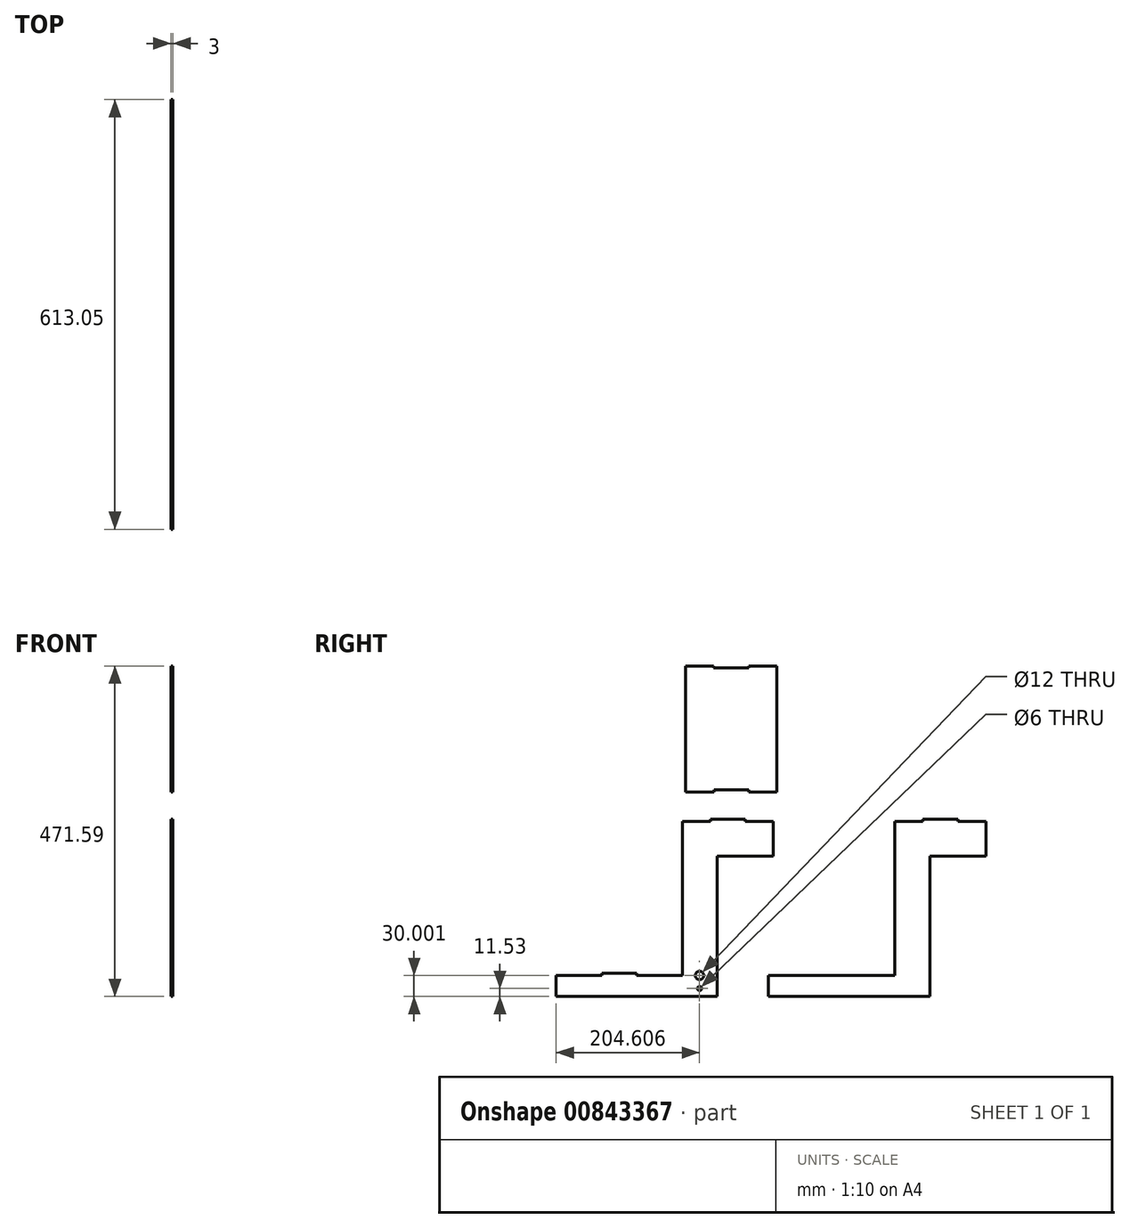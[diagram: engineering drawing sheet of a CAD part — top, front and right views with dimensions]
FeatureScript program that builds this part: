
annotation { "Feature Type Name" : "Feature", "Feature Type Description" : "" }
export const myFeature = defineFeature(function(context is Context, id is Id, definition is map)
    precondition{}
    {
        {
            var Q0;
            Q0=qCreatedBy(makeId("Right.planeOp"),FACE);
            var sketch = newSketch(context, id + "F0", { "sketchPlane" : qUnion([Q0])});
            skLineSegment(sketch, "E0", {"start": v(0, 42.16) * mm, "end": v(40, 42.16) * mm});
            skLineSegment(sketch, "E1", {"start": v(130, 42.16) * mm, "end": v(130, -7.84) * mm});
            skLineSegment(sketch, "E2", {"start": v(50, -7.84) * mm, "end": v(130, -7.84) * mm});
            skLineSegment(sketch, "E3", {"start": v(50, -7.84) * mm, "end": v(50, -207.84) * mm});
            skLineSegment(sketch, "E4", {"start": v(50, -207.84) * mm, "end": v(-180, -207.84) * mm});
            skLineSegment(sketch, "E5", {"start": v(-180, -207.84) * mm, "end": v(-180, -177.84) * mm});
            skLineSegment(sketch, "E6", {"start": v(0, -177.84) * mm, "end": v(-180, -177.84) * mm});
            skLineSegment(sketch, "E7", {"start": v(0, -177.84) * mm, "end": v(0, 42.16) * mm});
            skLineSegment(sketch, "E8", {"start": v(-298.05, 42.16) * mm, "end": v(-263.05, 42.16) * mm});
            skLineSegment(sketch, "E9", {"start": v(-173.05, 37.16) * mm, "end": v(-173.05, -2.84) * mm});
            skLineSegment(sketch, "E10", {"start": v(-248.05, -7.84) * mm, "end": v(-178.05, -7.84) * mm});
            skLineSegment(sketch, "E11", {"start": v(-253.05, -12.84) * mm, "end": v(-253.05, -207.84) * mm});
            skLineSegment(sketch, "E12", {"start": v(-253.05, -207.84) * mm, "end": v(-483.05, -207.84) * mm});
            skLineSegment(sketch, "E13", {"start": v(-483.05, -207.84) * mm, "end": v(-483.05, -177.84) * mm});
            skLineSegment(sketch, "E14", {"start": v(-303.05, -177.84) * mm, "end": v(-368.05, -177.84) * mm});
            skLineSegment(sketch, "E15", {"start": v(-303.05, -177.84) * mm, "end": v(-303.05, 37.16) * mm});
            skCircle(sketch, "E16", {"center": v(-278.44, -177.84) * mm, "radius": 6 * mm});
            skLineSegment(sketch, "E17.bottom", {"start": v(-298.36, 83.75) * mm, "end": v(-258.01, 83.75) * mm});
            skLineSegment(sketch, "E17.left", {"start": v(-298.36, 83.75) * mm, "end": v(-298.36, 263.75) * mm});
            skLineSegment(sketch, "E17.right", {"start": v(-168.36, 83.75) * mm, "end": v(-168.36, 263.75) * mm});
            skCircle(sketch, "E18", {"center": v(-278.44, -196.31) * mm, "radius": 3 * mm});
            skLineSegment(sketch, "E19", {"start": v(-263.05, 42.16) * mm, "end": v(-263.05, 45.16) * mm});
            skLineSegment(sketch, "E20", {"start": v(-263.05, 45.16) * mm, "end": v(-213.05, 45.16) * mm});
            skLineSegment(sketch, "E21", {"start": v(-213.05, 45.16) * mm, "end": v(-213.05, 42.16) * mm});
            skLineSegment(sketch, "E22.trimOffspring", {"start": v(-213.05, 42.16) * mm, "end": v(-178.05, 42.16) * mm});
            skLineSegment(sketch, "E23.top", {"start": v(-258.01, 86.75) * mm, "end": v(-208.01, 86.75) * mm});
            skLineSegment(sketch, "E23.left", {"start": v(-258.01, 83.75) * mm, "end": v(-258.01, 86.75) * mm});
            skLineSegment(sketch, "E23.right", {"start": v(-208.01, 83.75) * mm, "end": v(-208.01, 86.75) * mm});
            skLineSegment(sketch, "E24.trimOffspring", {"start": v(-208.01, 83.75) * mm, "end": v(-168.36, 83.75) * mm});
            skPoint(sketch, "E25.visualSharp", {"position": v(-303.05, 42.16) * mm});
            skPoint(sketch, "E26.visualSharp", {"position": v(-173.05, 42.16) * mm});
            skPoint(sketch, "E27.visualSharp", {"position": v(-173.05, -7.84) * mm});
            skPoint(sketch, "E28.visualSharp", {"position": v(-253.05, -7.84) * mm});
            skLineSegment(sketch, "E29", {"start": v(-483.05, -177.84) * mm, "end": v(-418.05, -177.84) * mm});
            skLineSegment(sketch, "E30", {"start": v(-418.05, -177.84) * mm, "end": v(-418.05, -174.84) * mm});
            skLineSegment(sketch, "E31", {"start": v(-418.05, -174.84) * mm, "end": v(-368.05, -174.84) * mm});
            skLineSegment(sketch, "E32", {"start": v(-368.05, -174.84) * mm, "end": v(-368.05, -177.84) * mm});
            skLineSegment(sketch, "E33.trimOffspring", {"start": v(-418.05, -177.84) * mm, "end": v(-483.05, -177.84) * mm});
            skLineSegment(sketch, "E34", {"start": v(-303.05, 37.16) * mm, "end": v(-303.05, 42.16) * mm});
            skLineSegment(sketch, "E35", {"start": v(-303.05, 42.16) * mm, "end": v(-298.05, 42.16) * mm});
            skLineSegment(sketch, "E36", {"start": v(-173.05, -2.84) * mm, "end": v(-173.05, -7.84) * mm});
            skLineSegment(sketch, "E37", {"start": v(-178.05, -7.84) * mm, "end": v(-173.05, -7.84) * mm});
            skLineSegment(sketch, "E38", {"start": v(-248.05, -7.84) * mm, "end": v(-253.05, -7.84) * mm});
            skLineSegment(sketch, "E39", {"start": v(-253.05, -12.84) * mm, "end": v(-253.05, -7.84) * mm});
            skLineSegment(sketch, "E40", {"start": v(-178.05, 42.16) * mm, "end": v(-173.05, 42.16) * mm});
            skLineSegment(sketch, "E41", {"start": v(-173.05, 42.16) * mm, "end": v(-173.05, 37.16) * mm});
            skLineSegment(sketch, "E42", {"start": v(-298.36, 263.75) * mm, "end": v(-258.36, 263.75) * mm});
            skLineSegment(sketch, "E43", {"start": v(-258.36, 263.75) * mm, "end": v(-258.36, 260.75) * mm});
            skLineSegment(sketch, "E44", {"start": v(-258.36, 260.75) * mm, "end": v(-208.36, 260.75) * mm});
            skLineSegment(sketch, "E45", {"start": v(-208.36, 260.75) * mm, "end": v(-208.36, 263.75) * mm});
            skLineSegment(sketch, "E46.trimOffspring", {"start": v(-208.36, 263.75) * mm, "end": v(-168.36, 263.75) * mm});
            skLineSegment(sketch, "E47", {"start": v(40, 42.16) * mm, "end": v(40, 45.16) * mm});
            skLineSegment(sketch, "E48", {"start": v(40, 45.16) * mm, "end": v(90, 45.16) * mm});
            skLineSegment(sketch, "E49", {"start": v(90, 45.16) * mm, "end": v(90, 42.16) * mm});
            skLineSegment(sketch, "E50.trimOffspring", {"start": v(90, 42.16) * mm, "end": v(130, 42.16) * mm});
            skLineSegment(sketch, "E51", {"start": v(-232, -173.43) * mm, "end": v(-167.15, -177.84) * mm});
            skSolve(sketch);
        }
        {
            var Q0;
            Q0=makeQuery(id+"F0.imprint","IMPRINT",FACE,{"disambiguationData":[TD([[makeQuery(id+"F0.imprint","IMPRINT",EDGE,{"derivedFrom":sQuery(id+"F0.wireOp",EDGE,"E0")}),-1.0]])]});
            var Q1;
            Q1=makeQuery(id+"F0.imprint","IMPRINT",FACE,{"disambiguationData":[TD([[makeQuery(id+"F0.imprint","IMPRINT",EDGE,{"derivedFrom":sQuery(id+"F0.wireOp",EDGE,"E8")}),-1.0]])]});
            var Q2;
            Q2=makeQuery(id+"F0.imprint","IMPRINT",FACE,{"disambiguationData":[TD([[makeQuery(id+"F0.imprint","IMPRINT",EDGE,{"derivedFrom":sQuery(id+"F0.wireOp",EDGE,"E17.bottom")}),1.0]])]});
            extrude(context, id + "F1", {"entities" : qUnion([Q0, Q1, Q2]), "oppositeDirection" : true, "depth" : 3 * mm, "offsetDistance" : 25 * mm});
        }
    });
